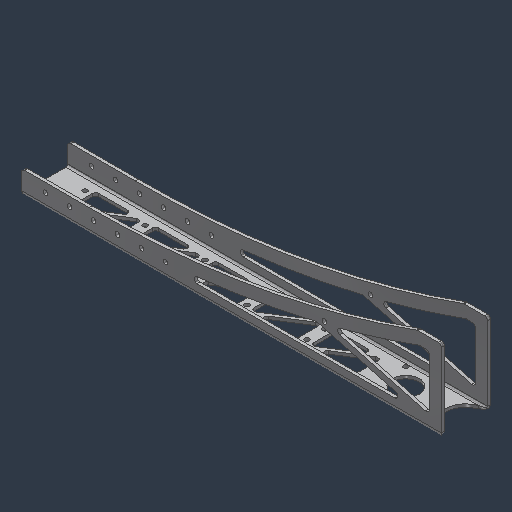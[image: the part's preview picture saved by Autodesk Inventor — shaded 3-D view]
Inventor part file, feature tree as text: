
AUTODESK INVENTOR PART (.ipt)
format: ipt  version: 2024.3 (Build 283343000, 343)  size: 551,936 bytes
history: native  units: mm (DEFAULTED — no unit token found)
features: sketch x5, hole x5, other x4, sheet_metal_op x3, chamfer x2, pattern_linear x2, plane x1, mirror x1
ambient origin geometry x8: Origin, YZ Plane, XZ Plane, XY Plane, X Axis, Y Axis, Z Axis, Center Point
bodies: Solid1 (feature_tree)
feature tree (23):
  plane  "Work Plane1"
  sheet_metal_op  "Face1"
  mirror  "Mirror1"
  sketch  "Sketch3"  dims[d9=22.86mm d10=2.032mm d11=3.175mm]
  sheet_metal_op  "Face2"
  chamfer  "Corner Round1"
  chamfer  "Corner Round2"
  hole  "Hole1"  [1 undecoded]
  hole  "Hole2"  [1 undecoded]
  pattern_linear  "Rectangular Pattern2"  Spacing1=444.5mm  [1 undecoded]
  hole  "Hole3"  [1 undecoded]
  pattern_linear  "Rectangular Pattern3"  Spacing1=25.4mm  [1 undecoded]
  hole  "Hole4"  [1 undecoded]
  hole  "Hole5"  [1 undecoded]
  other  "Plate1"
  other  "Plate2"
  sheet_metal_op  "Bend1"
  sketch  "Sketch4"  dims[d12=1.5875mm]
  sketch  "Sketch5"  dims[d13=6.35mm]
  sketch  "Sketch6"  dims[d14=4.7625mm d16=444.5mm d18=86.6775mm d19=25.4mm d20=12.7mm d21=6.35mm d22=75.0deg d23=3.175mm d24=28.575mm d26=101.6mm d27=3.175mm d28=50.8mm d29=50.0mm d31=63.5mm d32=10.0mm d34=25.4mm d36=3.175mm d37=0.0mm d38=3.175mm d70=3.175mm d71=9.525mm d72=25.4mm d73=5.1054mm d74=19.05mm d75=9.779mm d76=1.9558mm d77=14.3117mm d78=3.175mm d79=20.594885mm d83=60.0mm d85=25.4mm d88=5.1054mm d89=19.05mm d90=9.779mm d91=6.35mm d92=14.3117mm d93=25.4mm d94=20.594885mm d95=1026.4775mm d96=123.825mm d97=19.05mm d99=5.1054mm d100=19.05mm d101=9.525mm d102=6.35mm d103=14.3117mm d104=25.4mm d105=20.594885mm d107=44.45mm d108=6.35mm d109=70.0mm d111=63.5mm d112=63.5mm d113=28.575mm d114=19.05mm d115=8.3312mm d116=5.1562mm d117=14.3117mm d118=3.175mm d119=20.594885mm d120=50.8mm d121=5.1054mm d122=19.05mm d123=9.525mm d124=4.826mm d125=14.3117mm d126=3.175mm d127=20.594885mm d128=45.0deg d129=50.8mm]
  sketch  "Sketch2"  dims[d1=596.9mm d2=50.8mm d4=152.4mm d5=1016.0mm d8=3.175mm]
  other  "Cut1"
  other  "Definition1"
note: 7 required parameter values undecoded (feature->parameter linkage not recoverable at this tier; creation-order binding heuristic only, values carry confidence <= 0.55)
